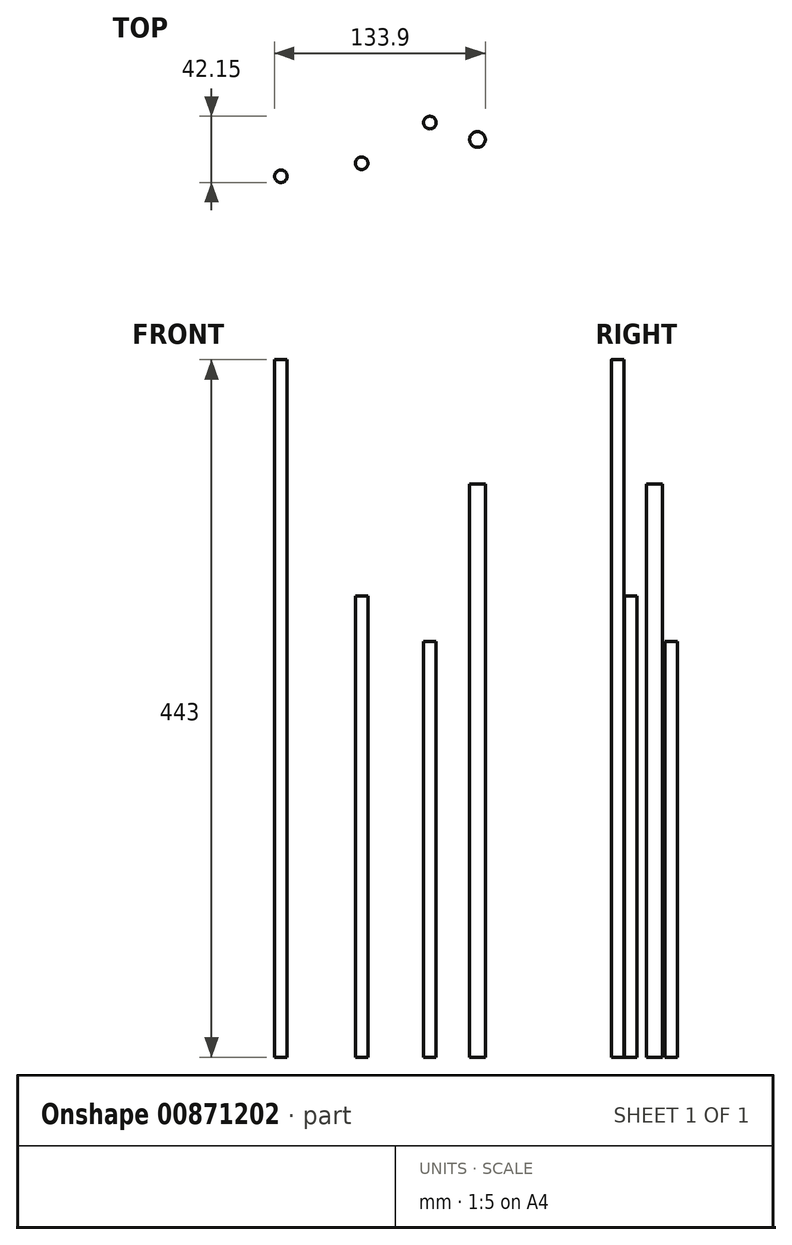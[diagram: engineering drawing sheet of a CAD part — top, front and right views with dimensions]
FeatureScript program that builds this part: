
annotation { "Feature Type Name" : "Feature", "Feature Type Description" : "" }
export const myFeature = defineFeature(function(context is Context, id is Id, definition is map)
    precondition{}
    {
        {
            var Q0;
            Q0=qCreatedBy(makeId("Top.planeOp"),FACE);
            var sketch = newSketch(context, id + "F0", { "sketchPlane" : qUnion([Q0])});
            skCircle(sketch, "E0", {"center": v(0, 0) * mm, "radius": 4 * mm});
            skSolve(sketch);
        }
        {
            var Q0;
            Q0 = qSketchRegion(id + "F0", true);
            extrude(context, id + "F1", {"entities" : qUnion([Q0]), "depth" : 443 * mm, "offsetDistance" : 25 * mm});
        }
        {
            var Q0;
            Q0=qCreatedBy(makeId("Top.planeOp"),FACE);
            var sketch = newSketch(context, id + "F2", { "sketchPlane" : qUnion([Q0])});
            skCircle(sketch, "E1", {"center": v(51.32, 8.3) * mm, "radius": 4 * mm});
            skSolve(sketch);
        }
        {
            var Q0;
            Q0=makeQuery(id+"F2.imprint","IMPRINT",FACE,{"disambiguationData":[TD([[makeQuery(id+"F2.imprint","IMPRINT",EDGE,{"derivedFrom":sQuery(id+"F2.wireOp",EDGE,"E1")}),1.0]])]});
            extrude(context, id + "F3", {"entities" : qUnion([Q0]), "depth" : 293 * mm, "offsetDistance" : 25 * mm});
        }
        {
            var Q0;
            Q0=qCreatedBy(makeId("Top.planeOp"),FACE);
            var sketch = newSketch(context, id + "F4", { "sketchPlane" : qUnion([Q0])});
            skCircle(sketch, "E2", {"center": v(94.66, 34.15) * mm, "radius": 4 * mm});
            skSolve(sketch);
        }
        {
            var Q0;
            Q0 = qSketchRegion(id + "F4", true);
            extrude(context, id + "F5", {"entities" : qUnion([Q0]), "depth" : (340 - 76) * mm, "offsetDistance" : 25 * mm});
        }
        {
            var Q0;
            Q0=qCreatedBy(makeId("Top.planeOp"),FACE);
            var sketch = newSketch(context, id + "F6", { "sketchPlane" : qUnion([Q0])});
            skCircle(sketch, "E3", {"center": v(124.9, 23.43) * mm, "radius": 5 * mm});
            skSolve(sketch);
        }
        {
            var Q0;
            Q0=makeQuery(id+"F6.imprint","IMPRINT",FACE,{"disambiguationData":[TD([[makeQuery(id+"F6.imprint","IMPRINT",EDGE,{"derivedFrom":sQuery(id+"F6.wireOp",EDGE,"E3")}),1.0]])]});
            extrude(context, id + "F7", {"entities" : qUnion([Q0]), "depth" : 364 * mm, "offsetDistance" : 25 * mm});
        }
    });
